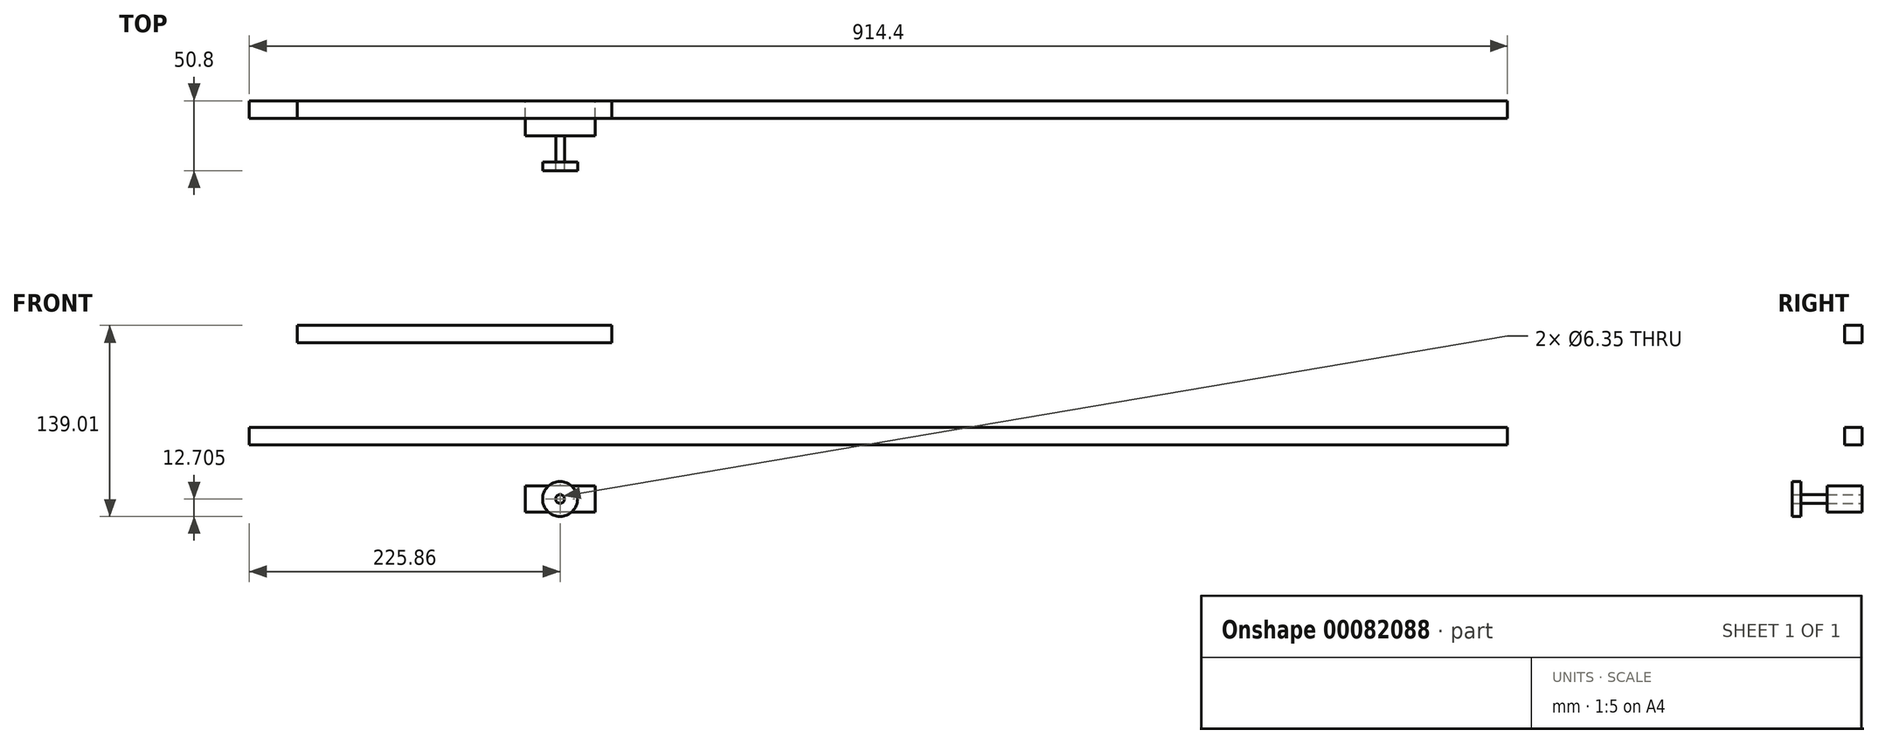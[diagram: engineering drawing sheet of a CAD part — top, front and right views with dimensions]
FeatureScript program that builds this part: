
annotation { "Feature Type Name" : "Feature", "Feature Type Description" : "" }
export const myFeature = defineFeature(function(context is Context, id is Id, definition is map)
    precondition{}
    {
        {
            var Q0;
            Q0=qCreatedBy(makeId("Front.planeOp"),FACE);
            var sketch = newSketch(context, id + "F0", { "sketchPlane" : qUnion([Q0])});
            skLineSegment(sketch, "E0.bottom", {"start": v(663.14, 42.46) * mm, "end": v(-251.26, 42.46) * mm});
            skLineSegment(sketch, "E0.top", {"start": v(663.14, 29.76) * mm, "end": v(-251.26, 29.76) * mm});
            skLineSegment(sketch, "E0.left", {"start": v(663.14, 42.46) * mm, "end": v(663.14, 29.76) * mm});
            skLineSegment(sketch, "E0.right", {"start": v(-251.26, 42.46) * mm, "end": v(-251.26, 29.76) * mm});
            skLineSegment(sketch, "E1.bottom", {"start": v(-216.42, 104.08) * mm, "end": v(12.18, 104.08) * mm});
            skLineSegment(sketch, "E1.top", {"start": v(-216.42, 116.78) * mm, "end": v(12.18, 116.78) * mm});
            skLineSegment(sketch, "E1.left", {"start": v(-216.42, 104.08) * mm, "end": v(-216.42, 116.78) * mm});
            skLineSegment(sketch, "E1.right", {"start": v(12.18, 104.08) * mm, "end": v(12.18, 116.78) * mm});
            skSolve(sketch);
        }
        {
            var Q0;
            Q0=makeQuery(id+"F0.imprint","IMPRINT",FACE,{"disambiguationData":[TD([[makeQuery(id+"F0.imprint","IMPRINT",EDGE,{"derivedFrom":sQuery(id+"F0.wireOp",EDGE,"E0.bottom")}),1.0]])]});
            var Q1;
            Q1=makeQuery(id+"F0.imprint","IMPRINT",FACE,{"disambiguationData":[TD([[makeQuery(id+"F0.imprint","IMPRINT",EDGE,{"derivedFrom":sQuery(id+"F0.wireOp",EDGE,"E1.bottom")}),1.0]])]});
            extrude(context, id + "F1", {"entities" : qUnion([Q0, Q1]), "depth" : 12.7 * mm});
        }
        {
            var Q0;
            Q0=qCreatedBy(makeId("Front.planeOp"),FACE);
            var sketch = newSketch(context, id + "F2", { "sketchPlane" : qUnion([Q0])});
            skLineSegment(sketch, "E2.bottom", {"start": v(0, 0) * mm, "end": v(-50.8, 0) * mm});
            skLineSegment(sketch, "E2.top", {"start": v(0, -19.05) * mm, "end": v(-50.8, -19.05) * mm});
            skLineSegment(sketch, "E2.left", {"start": v(0, 0) * mm, "end": v(0, -19.05) * mm});
            skLineSegment(sketch, "E2.right", {"start": v(-50.8, 0) * mm, "end": v(-50.8, -19.05) * mm});
            skLineSegment(sketch, "E3", {"start": v(0, 0) * mm, "end": v(-50.8, -19.05) * mm, "construction": true});
            skCircle(sketch, "E4", {"center": v(-25.4, -9.53) * mm, "radius": 3.18 * mm});
            skSolve(sketch);
        }
        {
            var Q0;
            Q0=makeQuery(id+"F2.imprint","IMPRINT",FACE,{"disambiguationData":[TD([[makeQuery(id+"F2.imprint","IMPRINT",EDGE,{"derivedFrom":sQuery(id+"F2.wireOp",EDGE,"E2.bottom")}),1.0]])]});
            extrude(context, id + "F3", {"entities" : qUnion([Q0]), "depth" : 25.4 * mm});
        }
        {
            var Q0;
            Q0=makeQuery(id+"F3.opExtrude","CAP_FACE",FACE,{"disambiguationData":[OSD([sQuery(id+"F2.wireOp",EDGE,"E2.bottom"),sQuery(id+"F2.wireOp",EDGE,"E2.top"),sQuery(id+"F2.wireOp",EDGE,"E2.left"),sQuery(id+"F2.wireOp",EDGE,"E2.right"),sQuery(id+"F2.wireOp",EDGE,"E4")])],"isStart":false});
            var sketch = newSketch(context, id + "F4", { "sketchPlane" : qUnion([Q0])});
            skCircle(sketch, "E5.0", {"center": v(-25.4, -9.53) * mm, "radius": 3.18 * mm});
            skSolve(sketch);
        }
        {
            var Q0;
            Q0=makeQuery(id+"F4.imprint","IMPRINT",FACE,{"disambiguationData":[TD([[makeQuery(id+"F4.imprint","IMPRINT",EDGE,{"derivedFrom":sQuery(id+"F4.wireOp",EDGE,"E5.0")}),1.0]])]});
            extrude(context, id + "F5", {"entities" : qUnion([Q0]), "depth" : 19.05 * mm});
        }
        {
            var Q0;
            Q0=makeQuery(id+"F5.opExtrude","CAP_FACE",FACE,{"disambiguationData":[OSD([sQuery(id+"F4.wireOp",EDGE,"E5.0")])],"isStart":false});
            var sketch = newSketch(context, id + "F6", { "sketchPlane" : qUnion([Q0])});
            skCircle(sketch, "E6", {"center": v(-25.4, -9.53) * mm, "radius": 12.7 * mm});
            skSolve(sketch);
        }
        {
            var Q0;
            Q0=makeQuery(id+"F6.imprint","IMPRINT",FACE,{"disambiguationData":[TD([[makeQuery(id+"F6.imprint","IMPRINT",EDGE,{"derivedFrom":sQuery(id+"F6.wireOp",EDGE,"E6")}),1.0]])]});
            extrude(context, id + "F7", {"entities" : qUnion([Q0]), "depth" : 6.35 * mm});
        }
    });
